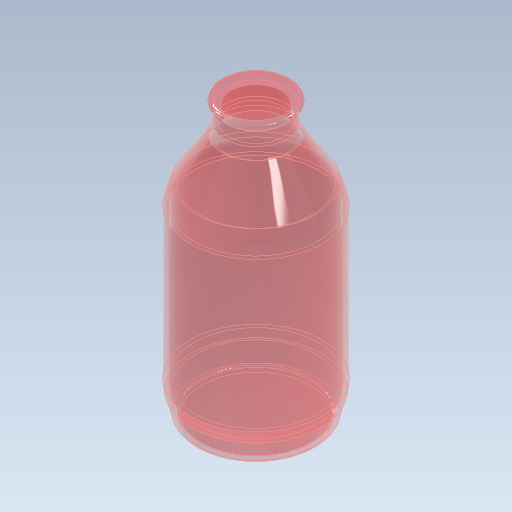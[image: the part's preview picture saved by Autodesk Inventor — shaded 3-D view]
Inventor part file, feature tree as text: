
AUTODESK INVENTOR PART (.ipt)
format: ipt  version: 2021 (Build 250183000, 183)  size: 229,888 bytes
history: native  units: mm
features: fillet x6, extrude x3, sketch x3, chamfer x2, shell x1
ambient origin geometry x8: Origin, YZ Plane, XZ Plane, XY Plane, X Axis, Y Axis, Z Axis, Center Point
bodies: Solid1 (feature_tree)
feature tree (15):
  extrude  "Extrusion1"  Depth=90.0mm TaperAngle=0.0deg
  chamfer  "Chamfer1"  Distance=10.0mm Angle=15.0deg
  chamfer  "Chamfer2"  Distance=12.5mm Angle=15.0deg
  extrude  "Extrusion2"  Depth=15.0mm
  fillet  "Fillet6"  Radius=3.0mm
  fillet  "Fillet5"  Radius=1.5mm
  fillet  "Fillet4"  Radius=0.5mm
  fillet  "Fillet3"  Radius=8.0mm
  shell  "Shell1"  Thickness=15.0mm
  extrude  "Extrusion3"  Depth=2.0mm
  fillet  "Fillet1"  Radius=1.5mm
  fillet  "Fillet2"  [1 undecoded]
  sketch  "Sketch1"  dims[d0=47.5mm d1=90.0mm d2=0.0mm d3=10.0mm d4=2.0mm d5=15.0deg d6=12.5mm d7=20.0mm d8=15.0deg]
  sketch  "Sketch2"  dims[d9=7.0mm d10=-0.872665mm d11=25.0mm d12=3.0mm d13=0.0mm d14=1.5mm d15=0.5mm d16=8.0mm d17=15.0mm]
  sketch  "Sketch3"  dims[d18=15.0mm d19=2.0mm d20=1.5mm]
note: 1 required parameter value undecoded (feature->parameter linkage not recoverable at this tier; creation-order binding heuristic only, values carry confidence <= 0.55)
